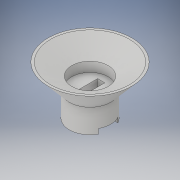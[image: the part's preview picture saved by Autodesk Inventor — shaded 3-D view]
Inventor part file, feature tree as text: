
AUTODESK INVENTOR PART (.ipt)
format: ipt  version: 2019 (Build 230136000, 136)  size: 147,456 bytes
history: native  units: in
note: dims shown in document units (in); Inventor stores cm internally (conversion verified against a paired STEP export)
features: sketch x4, extrude x3, revolve x1
ambient origin geometry x8: Origin, YZ Plane, XZ Plane, XY Plane, X Axis, Y Axis, Z Axis, Center Point
bodies: Solid1 (feature_tree)
feature tree (8):
  revolve  "Revolution1"  [1 undecoded]
  extrude  "Extrusion1"  Depth=0.3937in
  extrude  "Extrusion2"  Depth=0.0787in
  extrude  "Extrusion3"  Depth=0.2362in
  sketch  "Sketch2"  dims[d0=0.6693in d1=0.8661in]
  sketch  "Sketch3"  dims[d3=0.315in d4=0.3937in]
  sketch  "Sketch4"  dims[d5=1.3583in d6=0.0787in]
  sketch  "Sketch5"  dims[d7=90.0deg d8=0.2362in d9=0.7303in d10=0.5906in d11=0.0in d12=0.1181in d13=0.6299in d14=0.2756in d15=0.0in d16=0.1575in d17=0.0in]
note: 1 required parameter value undecoded (feature->parameter linkage not recoverable at this tier; creation-order binding heuristic only, values carry confidence <= 0.55)
